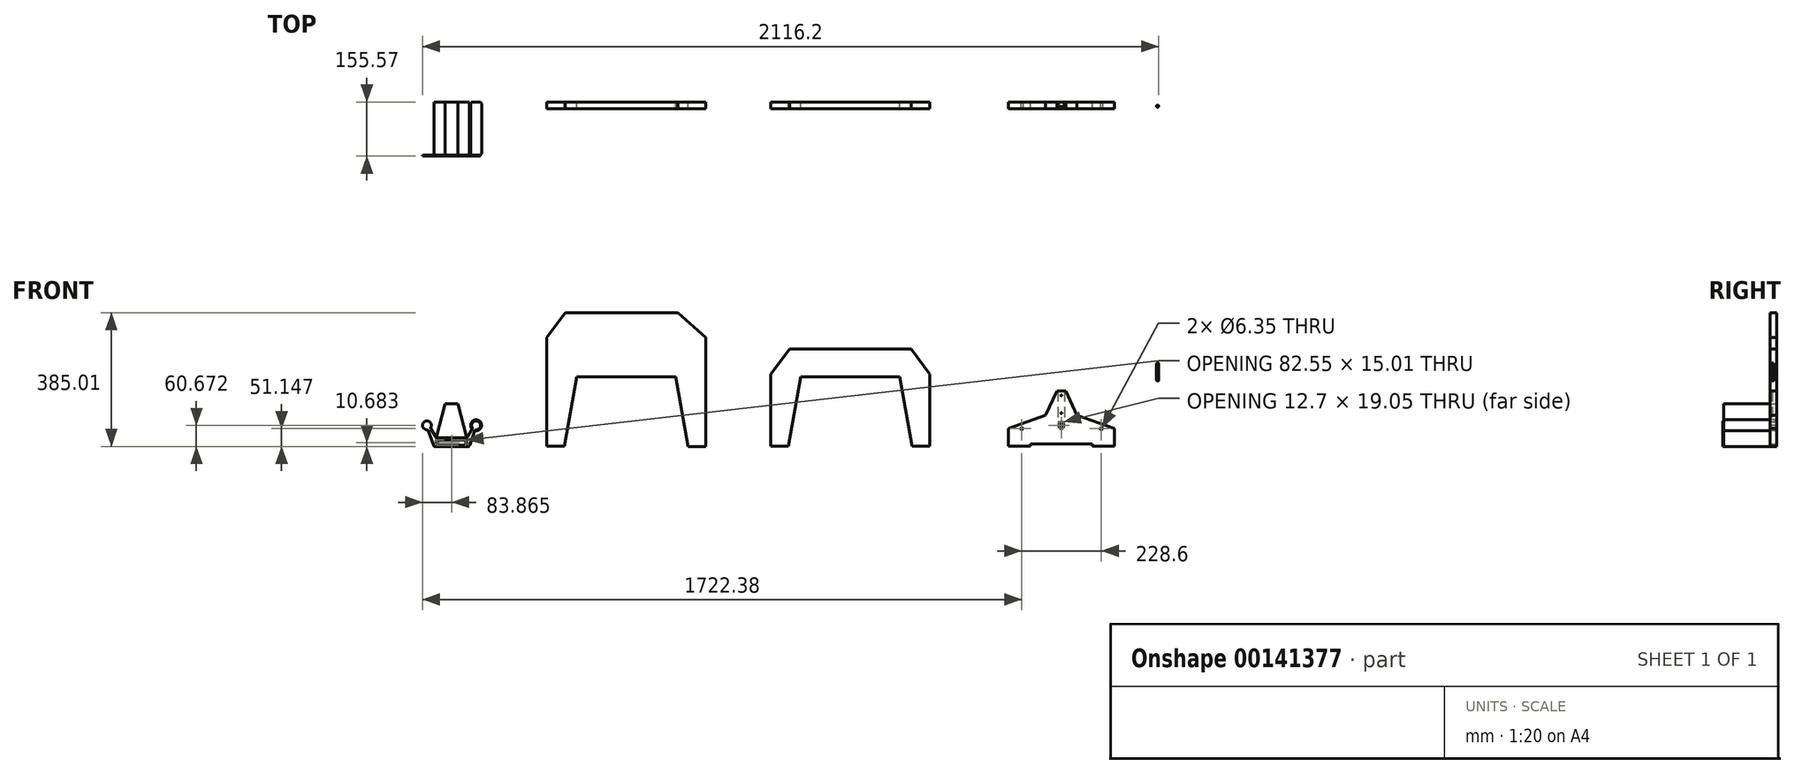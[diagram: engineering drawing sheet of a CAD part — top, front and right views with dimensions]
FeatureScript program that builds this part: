
annotation { "Feature Type Name" : "Feature", "Feature Type Description" : "" }
export const myFeature = defineFeature(function(context is Context, id is Id, definition is map)
    precondition{}
    {
        {
            var Q0;
            Q0=qCreatedBy(makeId("Front.planeOp"),FACE);
            var sketch = newSketch(context, id + "F0", { "sketchPlane" : qUnion([Q0])});
            skLineSegment(sketch, "E0", {"start": v(141.4, -188.6) * mm, "end": v(192.2, -188.6) * mm});
            skLineSegment(sketch, "E1", {"start": v(-214.2, -188.39) * mm, "end": v(-177.7, 11.5) * mm});
            skLineSegment(sketch, "E2", {"start": v(-177.7, 11.5) * mm, "end": v(106.11, 11.5) * mm});
            skLineSegment(sketch, "E3", {"start": v(106.11, 11.5) * mm, "end": v(141.4, -188.6) * mm});
            skLineSegment(sketch, "E4", {"start": v(-211.03, 196.2) * mm, "end": v(-265, 124.76) * mm});
            skLineSegment(sketch, "E5", {"start": v(112.82, 196.2) * mm, "end": v(192.2, 124.76) * mm});
            skLineSegment(sketch, "E6", {"start": v(-265, 124.76) * mm, "end": v(-265, -188.39) * mm});
            skLineSegment(sketch, "E7", {"start": v(192.2, 124.76) * mm, "end": v(192.2, -188.6) * mm});
            skLineSegment(sketch, "E8", {"start": v(-211.03, 196.2) * mm, "end": v(112.82, 196.2) * mm});
            skLineSegment(sketch, "E9", {"start": v(785.92, -188.4) * mm, "end": v(836.72, -188.4) * mm});
            skLineSegment(sketch, "E10", {"start": v(430.32, -188.39) * mm, "end": v(465.64, 11.72) * mm});
            skLineSegment(sketch, "E11", {"start": v(465.64, 11.72) * mm, "end": v(750.64, 11.72) * mm});
            skLineSegment(sketch, "E12", {"start": v(750.64, 11.72) * mm, "end": v(785.92, -188.4) * mm});
            skLineSegment(sketch, "E13", {"start": v(433.5, 91.01) * mm, "end": v(379.52, 19.58) * mm});
            skLineSegment(sketch, "E14", {"start": v(782.75, 91) * mm, "end": v(836.72, 19.57) * mm});
            skLineSegment(sketch, "E15", {"start": v(836.72, 19.57) * mm, "end": v(836.72, -188.4) * mm});
            skLineSegment(sketch, "E16", {"start": v(433.5, 91.01) * mm, "end": v(782.75, 91) * mm});
            skLineSegment(sketch, "E17", {"start": v(379.52, 19.58) * mm, "end": v(379.52, -188.39) * mm});
            skLineSegment(sketch, "E18", {"start": v(430.32, -188.39) * mm, "end": v(379.52, -188.39) * mm});
            skLineSegment(sketch, "E19.left", {"start": v(1062.38, -188.46) * mm, "end": v(1062.38, -137.66) * mm});
            skLineSegment(sketch, "E19.right", {"start": v(1125.88, -188.46) * mm, "end": v(1125.88, -182.11) * mm});
            skLineSegment(sketch, "E20.top", {"start": v(1303.5, -188.46) * mm, "end": v(1367, -188.46) * mm});
            skLineSegment(sketch, "E20.left", {"start": v(1303.5, -182.11) * mm, "end": v(1303.5, -188.46) * mm});
            skLineSegment(sketch, "E20.right", {"start": v(1367, -137.66) * mm, "end": v(1367, -188.46) * mm});
            skLineSegment(sketch, "E21", {"start": v(1062.38, -137.66) * mm, "end": v(1169.79, -98.57) * mm});
            skLineSegment(sketch, "E22", {"start": v(1201.99, -29.5) * mm, "end": v(1227.39, -29.5) * mm});
            skLineSegment(sketch, "E23", {"start": v(1259.6, -98.57) * mm, "end": v(1367, -137.66) * mm});
            skLineSegment(sketch, "E24", {"start": v(1201.99, -29.5) * mm, "end": v(1169.79, -98.57) * mm});
            skLineSegment(sketch, "E25", {"start": v(1062.38, -188.46) * mm, "end": v(1125.88, -188.46) * mm});
            skLineSegment(sketch, "E26", {"start": v(1227.39, -29.5) * mm, "end": v(1259.6, -98.57) * mm});
            skLineSegment(sketch, "E27", {"start": v(1125.88, -182.11) * mm, "end": v(1303.5, -182.11) * mm});
            skLineSegment(sketch, "E28", {"start": v(-265, -188.39) * mm, "end": v(-214.2, -188.39) * mm});
            skSolve(sketch);
        }
        {
            var Q0;
            Q0 = qSketchRegion(id + "F0", true);
            extrude(context, id + "F1", {"entities" : qUnion([Q0]), "depth" : 19.05 * mm});
        }
        {
            var Q0;
            Q0=makeQuery(id+"F1.opExtrude","CAP_FACE",FACE,{"disambiguationData":[OSD([sQuery(id+"F0.wireOp",EDGE,"E19.left"),sQuery(id+"F0.wireOp",EDGE,"E19.right"),sQuery(id+"F0.wireOp",EDGE,"E20.top"),sQuery(id+"F0.wireOp",EDGE,"E20.left"),sQuery(id+"F0.wireOp",EDGE,"E20.right"),sQuery(id+"F0.wireOp",EDGE,"E21"),sQuery(id+"F0.wireOp",EDGE,"E22"),sQuery(id+"F0.wireOp",EDGE,"E23"),sQuery(id+"F0.wireOp",EDGE,"E24"),sQuery(id+"F0.wireOp",EDGE,"E25"),sQuery(id+"F0.wireOp",EDGE,"E26"),sQuery(id+"F0.wireOp",EDGE,"E27")])],"isStart":false});
            var sketch = newSketch(context, id + "F2", { "sketchPlane" : qUnion([Q0])});
            skCircle(sketch, "E29", {"center": v(1100.84, -137.66) * mm, "radius": 3.18 * mm});
            skCircle(sketch, "E30", {"center": v(1329.44, -137.66) * mm, "radius": 3.18 * mm});
            skCircle(sketch, "E31", {"center": v(1214.69, -131.31) * mm, "radius": 6.35 * mm});
            skCircle(sketch, "E32", {"center": v(1214.69, -124.96) * mm, "radius": 6.35 * mm});
            skSolve(sketch);
        }
        {
            var Q0;
            Q0 = qSketchRegion(id + "F2", true);
            var Q1;
            Q1=makeQuery(id+"F1.opExtrude","CAP_FACE",FACE,{"disambiguationData":[OSD([sQuery(id+"F0.wireOp",EDGE,"E19.left"),sQuery(id+"F0.wireOp",EDGE,"E19.right"),sQuery(id+"F0.wireOp",EDGE,"E20.top"),sQuery(id+"F0.wireOp",EDGE,"E20.left"),sQuery(id+"F0.wireOp",EDGE,"E20.right"),sQuery(id+"F0.wireOp",EDGE,"E21"),sQuery(id+"F0.wireOp",EDGE,"E22"),sQuery(id+"F0.wireOp",EDGE,"E23"),sQuery(id+"F0.wireOp",EDGE,"E24"),sQuery(id+"F0.wireOp",EDGE,"E25"),sQuery(id+"F0.wireOp",EDGE,"E26"),sQuery(id+"F0.wireOp",EDGE,"E27")])],"isStart":true});
            extrude(context, id + "F3", {"entities" : qUnion([Q0]), "operationType" : NewBodyOperationType.REMOVE, "endBound" : BoundingType.UP_TO_SURFACE, "oppositeDirection" : true, "endBoundEntityFace" : qUnion([Q1]), "depth" : 25.4 * mm});
        }
        {
            var Q0;
            Q0=makeQuery(id+"F1.opExtrude","CAP_FACE",FACE,{"disambiguationData":[OSD([sQuery(id+"F0.wireOp",EDGE,"E19.left"),sQuery(id+"F0.wireOp",EDGE,"E19.right"),sQuery(id+"F0.wireOp",EDGE,"E20.top"),sQuery(id+"F0.wireOp",EDGE,"E20.left"),sQuery(id+"F0.wireOp",EDGE,"E20.right"),sQuery(id+"F0.wireOp",EDGE,"E21"),sQuery(id+"F0.wireOp",EDGE,"E22"),sQuery(id+"F0.wireOp",EDGE,"E23"),sQuery(id+"F0.wireOp",EDGE,"E24"),sQuery(id+"F0.wireOp",EDGE,"E25"),sQuery(id+"F0.wireOp",EDGE,"E26"),sQuery(id+"F0.wireOp",EDGE,"E27")])],"isStart":true});
            var sketch = newSketch(context, id + "F4", { "sketchPlane" : qUnion([Q0])});
            skLineSegment(sketch, "E33.bottom", {"start": v(-1224.21, -29.5) * mm, "end": v(-1205.16, -29.5) * mm});
            skLineSegment(sketch, "E33.top", {"start": v(-1224.21, -118.4) * mm, "end": v(-1205.16, -118.4) * mm});
            skLineSegment(sketch, "E33.left", {"start": v(-1224.21, -29.5) * mm, "end": v(-1224.21, -118.4) * mm});
            skLineSegment(sketch, "E33.right", {"start": v(-1205.16, -29.5) * mm, "end": v(-1205.16, -118.4) * mm});
            skSolve(sketch);
        }
        {
            var Q0;
            Q0 = qSketchRegion(id + "F4", true);
            extrude(context, id + "F5", {"entities" : qUnion([Q0]), "operationType" : NewBodyOperationType.REMOVE, "oppositeDirection" : true, "depth" : 12.7 * mm});
        }
        {
            var Q0;
            Q0=makeQuery(id+"F5.boolean.opBoolean","COPY",FACE,{"derivedFrom":makeQuery(id+"F5.opExtrude","CAP_FACE",FACE,{"disambiguationData":[OSD([sQuery(id+"F4.wireOp",EDGE,"E33.bottom"),sQuery(id+"F4.wireOp",EDGE,"E33.top"),sQuery(id+"F4.wireOp",EDGE,"E33.left"),sQuery(id+"F4.wireOp",EDGE,"E33.right")])],"isStart":false})});
            var sketch = newSketch(context, id + "F6", { "sketchPlane" : qUnion([Q0])});
            skCircle(sketch, "E34", {"center": v(-1214.69, -42.2) * mm, "radius": 1.59 * mm});
            skCircle(sketch, "E35", {"center": v(-1214.69, -93) * mm, "radius": 1.59 * mm});
            skSolve(sketch);
        }
        {
            var Q0;
            Q0 = qSketchRegion(id + "F6", true);
            var Q1;
            Q1=makeQuery(id+"F1.opExtrude","CAP_FACE",FACE,{"disambiguationData":[OSD([sQuery(id+"F0.wireOp",EDGE,"E19.left"),sQuery(id+"F0.wireOp",EDGE,"E19.right"),sQuery(id+"F0.wireOp",EDGE,"E20.top"),sQuery(id+"F0.wireOp",EDGE,"E20.left"),sQuery(id+"F0.wireOp",EDGE,"E20.right"),sQuery(id+"F0.wireOp",EDGE,"E21"),sQuery(id+"F0.wireOp",EDGE,"E22"),sQuery(id+"F0.wireOp",EDGE,"E23"),sQuery(id+"F0.wireOp",EDGE,"E24"),sQuery(id+"F0.wireOp",EDGE,"E25"),sQuery(id+"F0.wireOp",EDGE,"E26"),sQuery(id+"F0.wireOp",EDGE,"E27")])],"isStart":false});
            extrude(context, id + "F7", {"entities" : qUnion([Q0]), "operationType" : NewBodyOperationType.REMOVE, "endBound" : BoundingType.UP_TO_SURFACE, "oppositeDirection" : true, "endBoundEntityFace" : qUnion([Q1]), "depth" : 25.4 * mm});
        }
        {
            var Q0;
            Q0=qCreatedBy(makeId("Top.planeOp"),FACE);
            var sketch = newSketch(context, id + "F8", { "sketchPlane" : qUnion([Q0])});
            skCircle(sketch, "E36", {"center": v(1491.49, -12) * mm, "radius": 3.18 * mm});
            skSolve(sketch);
        }
        {
            var Q0;
            Q0 = qSketchRegion(id + "F8", true);
            extrude(context, id + "F9", {"entities" : qUnion([Q0]), "depth" : 50.8 * mm});
        }
        {
            var Q0;
            Q0=makeQuery(id+"F9.opExtrude","CAP_EDGE",EDGE,{"disambiguationData":[OSD([sQuery(id+"F8.wireOp",EDGE,"E36")])],"isStart":false});
            var Q1;
            Q1=makeQuery(id+"F9.opExtrude","CAP_EDGE",EDGE,{"disambiguationData":[OSD([sQuery(id+"F8.wireOp",EDGE,"E36")])],"isStart":true});
            chamfer(context, id + "F10", {"entities" : qUnion([Q0, Q1]), "width" : 0.8 * mm, "tangentPropagation" : true});
        }
        {
            var Q0;
            Q0=qCreatedBy(makeId("Front.planeOp"),FACE);
            var sketch = newSketch(context, id + "F11", { "sketchPlane" : qUnion([Q0])});
            skLineSegment(sketch, "E37", {"start": v(-487.42, -188.8) * mm, "end": v(-589.02, -188.8) * mm});
            skLineSegment(sketch, "E38", {"start": v(-589.02, -188.8) * mm, "end": v(-556.15, -66.13) * mm});
            skLineSegment(sketch, "E39", {"start": v(-520.3, -66.13) * mm, "end": v(-487.42, -188.8) * mm});
            skLineSegment(sketch, "E40", {"start": v(-556.15, -66.13) * mm, "end": v(-520.29, -66.13) * mm});
            skSolve(sketch);
        }
        {
            var Q0;
            Q0=makeQuery(id+"F11.imprint","IMPRINT",FACE,{"disambiguationData":[TD([[makeQuery(id+"F11.imprint","IMPRINT",EDGE,{"derivedFrom":sQuery(id+"F11.wireOp",EDGE,"E37")}),-1.0]])]});
            extrude(context, id + "F12", {"entities" : qUnion([Q0]), "depth" : 152.4 * mm});
        }
        {
            var Q0;
            Q0=makeQuery(id+"F12.opExtrude","CAP_FACE",FACE,{"disambiguationData":[OSD([sQuery(id+"F11.wireOp",EDGE,"E37"),sQuery(id+"F11.wireOp",EDGE,"E38"),sQuery(id+"F11.wireOp",EDGE,"E39"),sQuery(id+"F11.wireOp",EDGE,"E40")])],"isStart":false});
            var sketch = newSketch(context, id + "F13", { "sketchPlane" : qUnion([Q0])});
            skLineSegment(sketch, "E41", {"start": v(-589.02, -188.8) * mm, "end": v(-487.42, -188.8) * mm});
            skLineSegment(sketch, "E42", {"start": v(-494, -164.27) * mm, "end": v(-582.45, -164.27) * mm});
            skLineSegment(sketch, "E43", {"start": v(-606.14, -140.37) * mm, "end": v(-589.02, -188.8) * mm});
            skLineSegment(sketch, "E44", {"start": v(-598.97, -135.95) * mm, "end": v(-582.45, -164.27) * mm});
            skLineSegment(sketch, "E45.MirrorCS", {"start": v(-477.47, -135.95) * mm, "end": v(-494, -164.27) * mm});
            skLineSegment(sketch, "E46.MirrorCS", {"start": v(-470.3, -140.37) * mm, "end": v(-487.42, -188.8) * mm});
            skLineSegment(sketch, "E47.bottom", {"start": v(-578.95, -170.62) * mm, "end": v(-496.4, -170.62) * mm});
            skLineSegment(sketch, "E47.top", {"start": v(-578.95, -185.63) * mm, "end": v(-496.4, -185.63) * mm});
            skLineSegment(sketch, "E47.left", {"start": v(-578.95, -170.62) * mm, "end": v(-578.95, -185.63) * mm});
            skLineSegment(sketch, "E47.right", {"start": v(-496.4, -170.62) * mm, "end": v(-496.4, -185.63) * mm});
            skArc(sketch, "E48", {"start": v(-598.97, -135.95) * mm, "mid": v(-615.5, -117.14) * mm, "end": v(-606.14, -140.37) * mm});
            skArc(sketch, "E49", {"start": v(-477.47, -135.95) * mm, "mid": v(-460.94, -117.14) * mm, "end": v(-470.3, -140.37) * mm});
            skSolve(sketch);
        }
        {
            var Q0;
            Q0 = qSketchRegion(id + "F13", true);
            extrude(context, id + "F14", {"entities" : qUnion([Q0]), "depth" : 3.17 * mm});
        }
        {
            var Q0;
            Q0=makeQuery(id+"F14.opExtrude","SWEPT_EDGE",EDGE,{"disambiguationData":[OSD([sQuery(id+"F13.wireOp",EDGE,"E44"),sQuery(id+"F13.wireOp",EDGE,"E48")])]});
            var Q1;
            Q1=makeQuery(id+"F14.opExtrude","SWEPT_EDGE",EDGE,{"disambiguationData":[OSD([sQuery(id+"F13.wireOp",EDGE,"E43"),sQuery(id+"F13.wireOp",EDGE,"E48")])]});
            var Q2;
            Q2=makeQuery(id+"F14.opExtrude","SWEPT_EDGE",EDGE,{"disambiguationData":[OSD([sQuery(id+"F11.wireOp",EDGE,"E38"),sQuery(id+"F13.wireOp",EDGE,"E42"),sQuery(id+"F13.wireOp",EDGE,"E44")])]});
            var Q3;
            Q3=makeQuery(id+"F14.opExtrude","SWEPT_EDGE",EDGE,{"disambiguationData":[OSD([sQuery(id+"F11.wireOp",EDGE,"E38"),sQuery(id+"F13.wireOp",EDGE,"E41"),sQuery(id+"F13.wireOp",EDGE,"E43")])]});
            var Q4;
            Q4=makeQuery(id+"F14.opExtrude","SWEPT_EDGE",EDGE,{"disambiguationData":[OSD([sQuery(id+"F13.wireOp",EDGE,"E47.bottom"),sQuery(id+"F13.wireOp",EDGE,"E47.left")])]});
            var Q5;
            Q5=makeQuery(id+"F14.opExtrude","SWEPT_EDGE",EDGE,{"disambiguationData":[OSD([sQuery(id+"F13.wireOp",EDGE,"E47.top"),sQuery(id+"F13.wireOp",EDGE,"E47.left")])]});
            var Q6;
            Q6=makeQuery(id+"F14.opExtrude","SWEPT_EDGE",EDGE,{"disambiguationData":[OSD([sQuery(id+"F13.wireOp",EDGE,"E47.bottom"),sQuery(id+"F13.wireOp",EDGE,"E47.right")])]});
            var Q7;
            Q7=makeQuery(id+"F14.opExtrude","SWEPT_EDGE",EDGE,{"disambiguationData":[OSD([sQuery(id+"F13.wireOp",EDGE,"E47.top"),sQuery(id+"F13.wireOp",EDGE,"E47.right")])]});
            var Q8;
            Q8=makeQuery(id+"F14.opExtrude","SWEPT_EDGE",EDGE,{"disambiguationData":[OSD([sQuery(id+"F11.wireOp",EDGE,"E39"),sQuery(id+"F13.wireOp",EDGE,"E42"),sQuery(id+"F13.wireOp",EDGE,"E45.MirrorCS")])]});
            var Q9;
            Q9=makeQuery(id+"F14.opExtrude","SWEPT_EDGE",EDGE,{"disambiguationData":[OSD([sQuery(id+"F11.wireOp",EDGE,"E39"),sQuery(id+"F13.wireOp",EDGE,"E41"),sQuery(id+"F13.wireOp",EDGE,"E46.MirrorCS")])]});
            var Q10;
            Q10=makeQuery(id+"F14.opExtrude","SWEPT_EDGE",EDGE,{"disambiguationData":[OSD([sQuery(id+"F13.wireOp",EDGE,"E46.MirrorCS"),sQuery(id+"F13.wireOp",EDGE,"E49")])]});
            var Q11;
            Q11=makeQuery(id+"F14.opExtrude","SWEPT_EDGE",EDGE,{"disambiguationData":[OSD([sQuery(id+"F13.wireOp",EDGE,"E45.MirrorCS"),sQuery(id+"F13.wireOp",EDGE,"E49")])]});
            fillet(context, id + "F15", {"entities" : qUnion([Q0, Q1, Q2, Q3, Q4, Q5, Q6, Q7, Q8, Q9, Q10, Q11]), "radius" : 5.08 * mm, "tangentPropagation" : true, "allowEdgeOverflow" : false});
        }
        {
            var Q0;
            Q0=makeQuery(id+"F14.opExtrude","CAP_FACE",FACE,{"disambiguationData":[OSD([sQuery(id+"F13.wireOp",EDGE,"E41"),sQuery(id+"F13.wireOp",EDGE,"E42"),sQuery(id+"F13.wireOp",EDGE,"E43"),sQuery(id+"F13.wireOp",EDGE,"E44"),sQuery(id+"F13.wireOp",EDGE,"E45.MirrorCS"),sQuery(id+"F13.wireOp",EDGE,"E46.MirrorCS"),sQuery(id+"F13.wireOp",EDGE,"E47.bottom"),sQuery(id+"F13.wireOp",EDGE,"E47.top"),sQuery(id+"F13.wireOp",EDGE,"E47.left"),sQuery(id+"F13.wireOp",EDGE,"E47.right"),sQuery(id+"F13.wireOp",EDGE,"E48"),sQuery(id+"F13.wireOp",EDGE,"E49")])],"isStart":true});
            var sketch = newSketch(context, id + "F16", { "sketchPlane" : qUnion([Q0])});
            skCircle(sketch, "E50", {"center": v(467.6, -127.96) * mm, "radius": 15.88 * mm});
            skSolve(sketch);
        }
        {
            var Q0;
            Q0 = qSketchRegion(id + "F16", true);
            extrude(context, id + "F17", {"entities" : qUnion([Q0]), "depth" : 152.4 * mm});
        }
        {
            var Q0;
            Q0=makeQuery(id+"F17.opExtrude","CAP_EDGE",EDGE,{"disambiguationData":[OSD([sQuery(id+"F16.wireOp",EDGE,"E50")])],"isStart":true});
            var Q1;
            Q1=makeQuery(id+"F17.opExtrude","CAP_EDGE",EDGE,{"disambiguationData":[OSD([sQuery(id+"F16.wireOp",EDGE,"aZfgL0ft-th2g-uMPH-NlW3-Ob5x9SX0eYJR")])],"isStart":true});
            var Q2;
            Q2=makeQuery(id+"F17.opExtrude","CAP_EDGE",EDGE,{"disambiguationData":[OSD([sQuery(id+"F16.wireOp",EDGE,"aZfgL0ft-th2g-uMPH-NlW3-Ob5x9SX0eYJR")])],"isStart":false});
            var Q3;
            Q3=makeQuery(id+"F17.opExtrude","CAP_EDGE",EDGE,{"disambiguationData":[OSD([sQuery(id+"F16.wireOp",EDGE,"E50")])],"isStart":false});
            fillet(context, id + "F18", {"entities" : qUnion([Q0, Q1, Q2, Q3]), "radius" : 6.35 * mm, "tangentPropagation" : true, "allowEdgeOverflow" : false});
        }
    });
